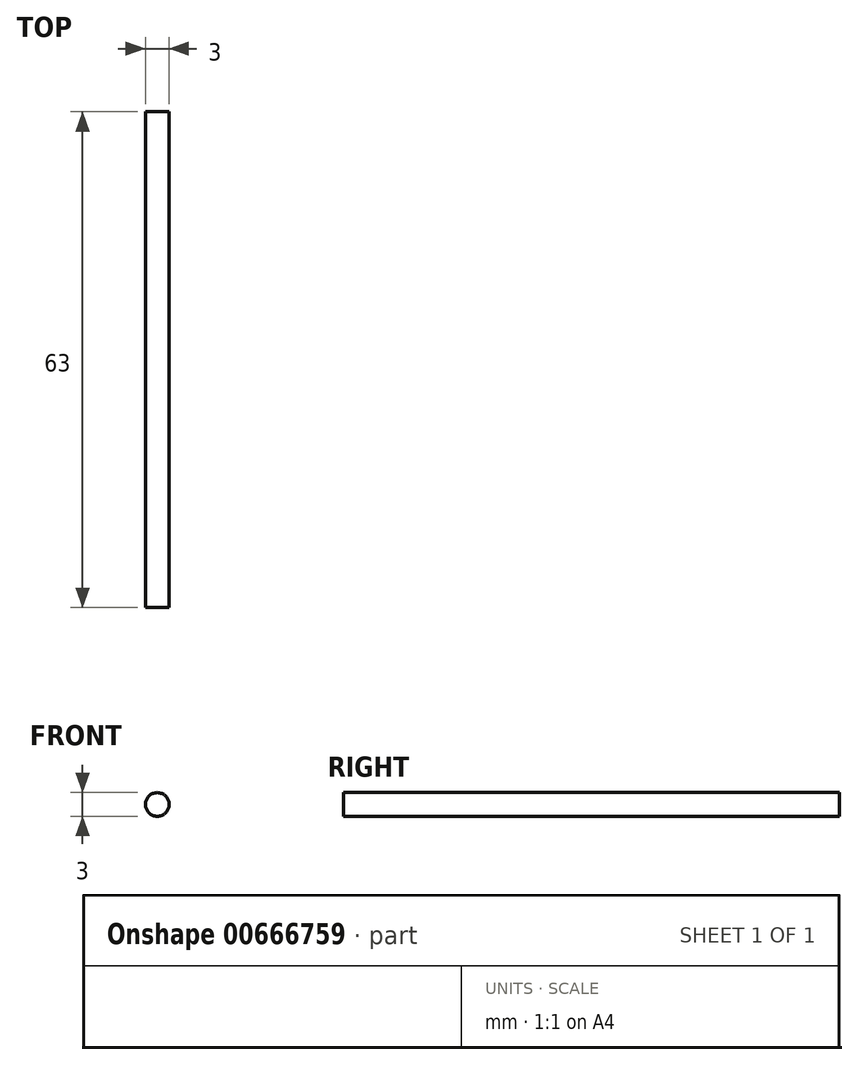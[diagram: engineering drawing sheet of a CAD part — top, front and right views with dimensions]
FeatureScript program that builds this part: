
annotation { "Feature Type Name" : "Feature", "Feature Type Description" : "" }
export const myFeature = defineFeature(function(context is Context, id is Id, definition is map)
    precondition{}
    {
        {
            var Q0;
            Q0=qCreatedBy(makeId("Front.planeOp"),FACE);
            var sketch = newSketch(context, id + "F0", { "sketchPlane" : qUnion([Q0])});
            skCircle(sketch, "E0", {"center": v(0, 0) * mm, "radius": 1.5 * mm});
            skSolve(sketch);
        }
        {
            var Q0;
            Q0=makeQuery(id+"F0.imprint","IMPRINT",FACE,{"disambiguationData":[TD([[makeQuery(id+"F0.imprint","IMPRINT",EDGE,{"derivedFrom":sQuery(id+"F0.wireOp",EDGE,"E0")}),1.0]])]});
            extrude(context, id + "F1", {"entities" : qUnion([Q0]), "depth" : 63 * mm, "offsetDistance" : 25 * mm});
        }
    });
